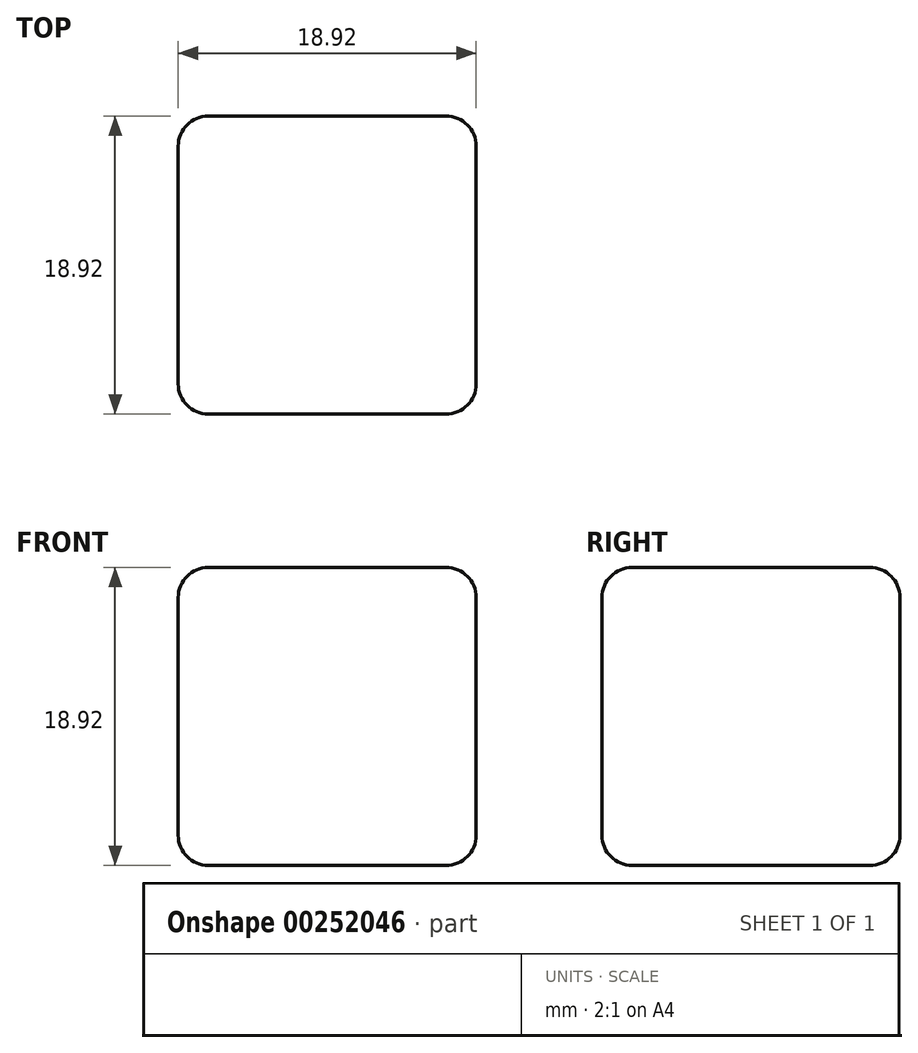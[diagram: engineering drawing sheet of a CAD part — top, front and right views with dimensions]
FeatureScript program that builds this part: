
annotation { "Feature Type Name" : "Feature", "Feature Type Description" : "" }
export const myFeature = defineFeature(function(context is Context, id is Id, definition is map)
    precondition{}
    {
        {
            var Q0;
            Q0=qCreatedBy(makeId("Front.planeOp"),FACE);
            var sketch = newSketch(context, id + "F0", { "sketchPlane" : qUnion([Q0])});
            skLineSegment(sketch, "E0.bottom", {"start": v(9.46, 9.46) * mm, "end": v(-9.46, 9.46) * mm});
            skLineSegment(sketch, "E0.top", {"start": v(9.46, -9.46) * mm, "end": v(-9.46, -9.46) * mm});
            skLineSegment(sketch, "E0.left", {"start": v(9.46, 9.46) * mm, "end": v(9.46, -9.46) * mm});
            skLineSegment(sketch, "E0.right", {"start": v(-9.46, 9.46) * mm, "end": v(-9.46, -9.46) * mm});
            skPoint(sketch, "E0.middle", {"position": v(0, 0) * mm});
            skSolve(sketch);
        }
        {
            var Q0;
            Q0=makeQuery(id+"F0.imprint","IMPRINT",FACE,{"disambiguationData":[TD([[makeQuery(id+"F0.imprint","IMPRINT",EDGE,{"derivedFrom":sQuery(id+"F0.wireOp",EDGE,"E0.bottom")}),1.0]])]});
            extrude(context, id + "F1", {"entities" : qUnion([Q0]), "endBound" : BoundingType.SYMMETRIC, "depth" : 18.92 * mm});
        }
        {
            var Q0;
            Q0=makeQuery(id+"F1.opExtrude","CAP_EDGE",EDGE,{"disambiguationData":[OSD([sQuery(id+"F0.wireOp",EDGE,"E0.left")])],"isStart":true});
            var Q1;
            Q1=makeQuery(id+"F1.opExtrude","CAP_EDGE",EDGE,{"disambiguationData":[OSD([sQuery(id+"F0.wireOp",EDGE,"E0.left")])],"isStart":false});
            var Q2;
            Q2=makeQuery(id+"F1.opExtrude","CAP_EDGE",EDGE,{"disambiguationData":[OSD([sQuery(id+"F0.wireOp",EDGE,"E0.right")])],"isStart":true});
            var Q3;
            Q3=makeQuery(id+"F1.opExtrude","CAP_EDGE",EDGE,{"disambiguationData":[OSD([sQuery(id+"F0.wireOp",EDGE,"E0.right")])],"isStart":false});
            var Q4;
            Q4=makeQuery(id+"F1.opExtrude","SWEPT_EDGE",EDGE,{"disambiguationData":[OSD([sQuery(id+"F0.wireOp",EDGE,"E0.bottom"),sQuery(id+"F0.wireOp",EDGE,"E0.right")])]});
            var Q5;
            Q5=makeQuery(id+"F1.opExtrude","SWEPT_EDGE",EDGE,{"disambiguationData":[OSD([sQuery(id+"F0.wireOp",EDGE,"E0.bottom"),sQuery(id+"F0.wireOp",EDGE,"E0.left")])]});
            var Q6;
            Q6=makeQuery(id+"F1.opExtrude","CAP_EDGE",EDGE,{"disambiguationData":[OSD([sQuery(id+"F0.wireOp",EDGE,"E0.bottom")])],"isStart":true});
            var Q7;
            Q7=makeQuery(id+"F1.opExtrude","CAP_EDGE",EDGE,{"disambiguationData":[OSD([sQuery(id+"F0.wireOp",EDGE,"E0.bottom")])],"isStart":false});
            var Q8;
            Q8=makeQuery(id+"F1.opExtrude","CAP_EDGE",EDGE,{"disambiguationData":[OSD([sQuery(id+"F0.wireOp",EDGE,"E0.top")])],"isStart":true});
            var Q9;
            Q9=makeQuery(id+"F1.opExtrude","SWEPT_EDGE",EDGE,{"disambiguationData":[OSD([sQuery(id+"F0.wireOp",EDGE,"E0.top"),sQuery(id+"F0.wireOp",EDGE,"E0.left")])]});
            var Q10;
            Q10=makeQuery(id+"F1.opExtrude","CAP_EDGE",EDGE,{"disambiguationData":[OSD([sQuery(id+"F0.wireOp",EDGE,"E0.top")])],"isStart":false});
            var Q11;
            Q11=makeQuery(id+"F1.opExtrude","SWEPT_EDGE",EDGE,{"disambiguationData":[OSD([sQuery(id+"F0.wireOp",EDGE,"E0.top"),sQuery(id+"F0.wireOp",EDGE,"E0.right")])]});
            fillet(context, id + "F2", {"entities" : qUnion([Q0, Q1, Q2, Q3, Q4, Q5, Q6, Q7, Q8, Q9, Q10, Q11]), "radius" : 1.9 * mm, "tangentPropagation" : true, "allowEdgeOverflow" : false});
        }
    });
